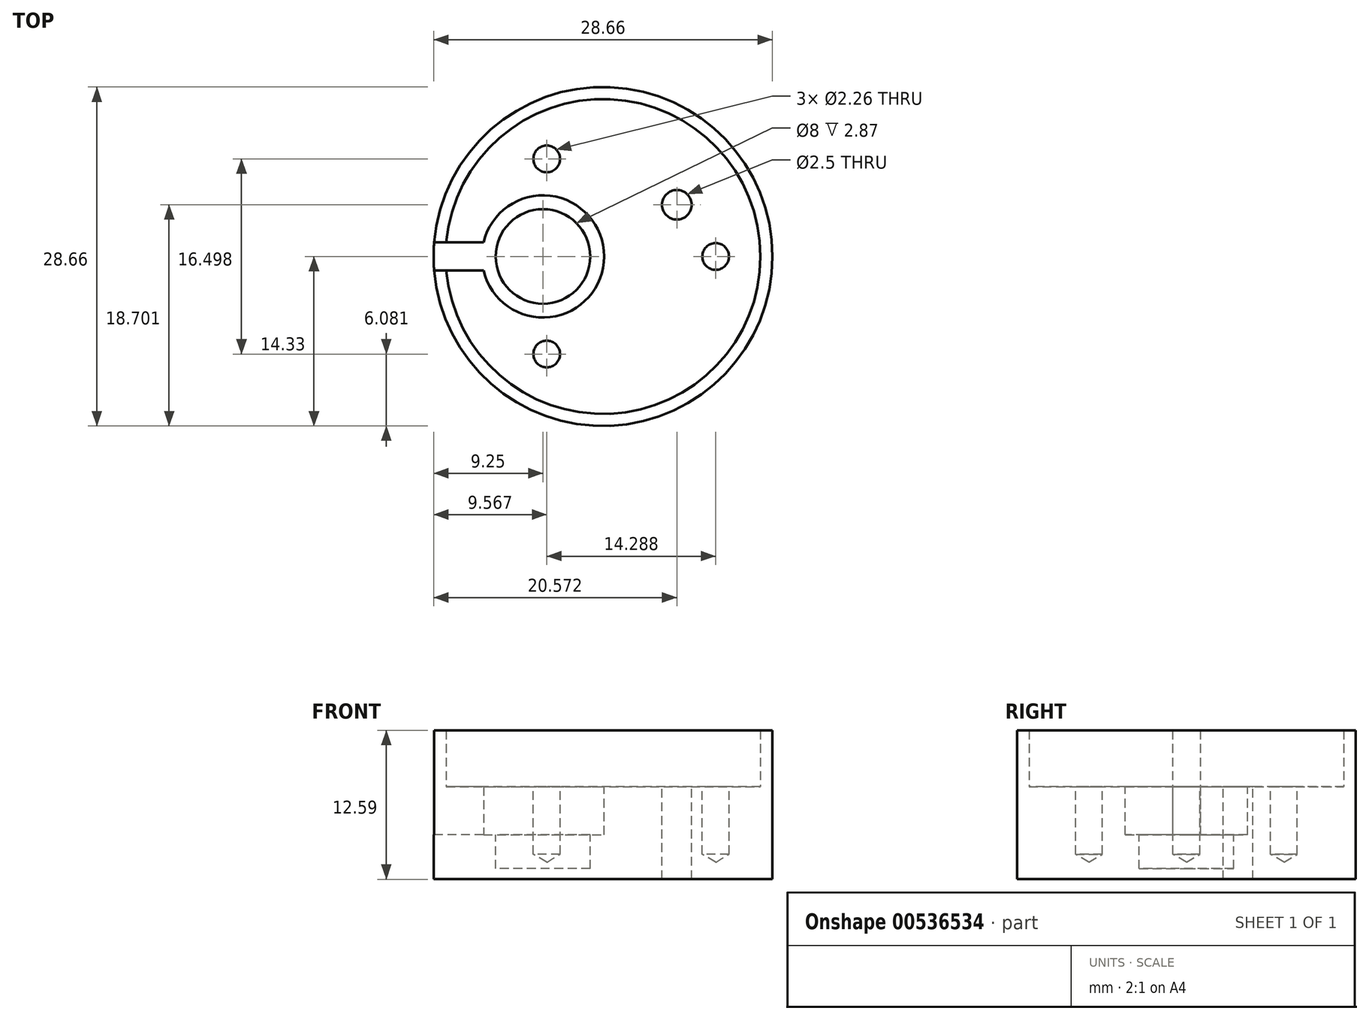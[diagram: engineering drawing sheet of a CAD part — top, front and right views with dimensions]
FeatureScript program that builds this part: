
annotation { "Feature Type Name" : "Feature", "Feature Type Description" : "" }
export const myFeature = defineFeature(function(context is Context, id is Id, definition is map)
    precondition{}
    {
        {
            var Q0;
            Q0=qCreatedBy(makeId("Front.planeOp"),FACE);
            var sketch = newSketch(context, id + "F0", { "sketchPlane" : qUnion([Q0])});
            skLineSegment(sketch, "E0", {"start": v(14.33, 0) * mm, "end": v(14.33, -12.59) * mm});
            skLineSegment(sketch, "E1", {"start": v(14.33, -12.59) * mm, "end": v(0, -12.59) * mm});
            skLineSegment(sketch, "E2", {"start": v(0, -12.59) * mm, "end": v(0, -4.76) * mm});
            skLineSegment(sketch, "E3", {"start": v(0, -4.76) * mm, "end": v(13.31, -4.76) * mm});
            skLineSegment(sketch, "E4", {"start": v(13.31, -4.76) * mm, "end": v(13.31, 0) * mm});
            skLineSegment(sketch, "E5", {"start": v(13.31, 0) * mm, "end": v(14.33, 0) * mm});
            skLineSegment(sketch, "E6", {"start": v(0, -12.59) * mm, "end": v(0, -26.31) * mm, "construction": true});
            skSolve(sketch);
        }
        {
            var Q0;
            Q0=qSketchRegion(id+"F0",true);
            var Q1;
            Q1=sQuery(id+"F0.wireOp",EDGE,"E2");
            revolve(context, id + "F1", {"entities" : qUnion([Q0]), "axis" : qUnion([Q1]), "revolveType" : RevolveType.FULL});
        }
        {
            var Q0;
            Q0=makeQuery(id+"F1.opRevolve","SWEPT_FACE",FACE,{"disambiguationData":[OSD([sQuery(id+"F0.wireOp",EDGE,"E3")])]});
            var sketch = newSketch(context, id + "F2", { "sketchPlane" : qUnion([Q0])});
            skPoint(sketch, "E7", {"position": v(9.52, 0) * mm});
            skPoint(sketch, "E8.1.0", {"position": v(-4.76, 8.25) * mm});
            skPoint(sketch, "E8.2.0", {"position": v(-4.76, -8.25) * mm});
            skPoint(sketch, "E8.center", {"position": v(0, 0) * mm});
            skSolve(sketch);
        }
        {
            var Q0;
            Q0=sQuery(id+"F2.wireOp",VERTEX,"E7");
            var Q1;
            Q1=sQuery(id+"F2.wireOp",VERTEX,"E8.1.0");
            var Q2;
            Q2=sQuery(id+"F2.wireOp",VERTEX,"E8.2.0");
            var Q3;
            Q3=makeQuery(id+"F1.opRevolve","SWEPT_BODY",BODY,{"disambiguationData":[OSD([sQuery(id+"F0.wireOp",EDGE,"E0"),sQuery(id+"F0.wireOp",EDGE,"E1"),sQuery(id+"F0.wireOp",EDGE,"E2"),sQuery(id+"F0.wireOp",EDGE,"E3"),sQuery(id+"F0.wireOp",EDGE,"E4"),sQuery(id+"F0.wireOp",EDGE,"E5"),sQuery(id+"F0.wireOp",EDGE,"N4qPm8u9-ntjg-4JQa-pogc-oRLvVNEznxfI"),sQuery(id+"F0.wireOp",EDGE,"MrgsN7Nr-Gjff-1Huv-wU94-kZHdJzqhYVDD"),sQuery(id+"F0.wireOp",EDGE,"Pg9PKC79-TiTN-lwUD-c8gR-E9RlHLgOT5QF"),sQuery(id+"F0.wireOp",EDGE,"fodt5jp9-1a0J-tqfQ-503d-72WKcELB2Erp")])]});
            hole(context, id + "F3", {"style" : HoleStyle.SIMPLE, "endStyle" : HoleEndStyle.BLIND, "standardTappedOrClearance" : lookupTablePath({ "standard" : "ANSI", "engagement" : "75%", "pitch" : "40 tpi", "size" : "#4", "type" : "Tapped" }), "standardBlindInLast" : lookupTablePath({ "standard" : "ANSI", "engagement" : "75%", "pitch" : "40 tpi", "size" : "#4", "type" : "Tapped" }), "holeDiameter" : 2.26 * mm, "majorDiameter" : 2.84 * mm, "showTappedDepth" : true, "holeDepth" : 5.72 * mm, "tappedDepth" : 5.08 * mm, "tapClearance" : 1, "startFromSketch" : true, "locations" : qUnion([Q0, Q1, Q2]), "scope" : qUnion([Q3])});
        }
        {
            var Q0;
            Q0=makeQuery(id+"F1.opRevolve","SWEPT_FACE",FACE,{"disambiguationData":[OSD([sQuery(id+"F0.wireOp",EDGE,"E3")])]});
            var sketch = newSketch(context, id + "F4", { "sketchPlane" : qUnion([Q0])});
            skLineSegment(sketch, "E9", {"start": v(0, 0) * mm, "end": v(-5.08, 0) * mm, "construction": true});
            skCircle(sketch, "E10", {"center": v(-5.08, 0) * mm, "radius": 5.17 * mm});
            skSolve(sketch);
        }
        {
            var Q0;
            Q0 = qSketchRegion(id + "F4", true);
            extrude(context, id + "F5", {"entities" : qUnion([Q0]), "operationType" : NewBodyOperationType.REMOVE, "oppositeDirection" : true, "depth" : 4.06 * mm, "offsetDistance" : 25.4 * mm});
        }
        {
            var Q0;
            Q0=makeQuery(id+"F5.boolean.opBoolean","COPY",FACE,{"derivedFrom":makeQuery(id+"F5.opExtrude","CAP_FACE",FACE,{"disambiguationData":[OSD([sQuery(id+"F4.wireOp",EDGE,"E10")])],"isStart":false})});
            var sketch = newSketch(context, id + "F6", { "sketchPlane" : qUnion([Q0])});
            skPoint(sketch, "E11", {"position": v(-5.08, 0) * mm});
            skCircle(sketch, "E12", {"center": v(-5.08, 0) * mm, "radius": 4 * mm});
            skSolve(sketch);
        }
        {
            var Q0;
            Q0=makeQuery(id+"F6.imprint","IMPRINT",FACE,{"disambiguationData":[TD([[makeQuery(id+"F6.imprint","IMPRINT",EDGE,{"derivedFrom":sQuery(id+"F6.wireOp",EDGE,"E12")}),1.0]])]});
            extrude(context, id + "F7", {"entities" : qUnion([Q0]), "operationType" : NewBodyOperationType.REMOVE, "oppositeDirection" : true, "depth" : 2.87 * mm, "offsetDistance" : 25.4 * mm});
        }
        {
            var Q0;
            Q0=makeQuery(id+"F5.boolean.opBoolean","COPY",FACE,{"derivedFrom":makeQuery(id+"F5.opExtrude","CAP_FACE",FACE,{"disambiguationData":[OSD([sQuery(id+"F4.wireOp",EDGE,"E10")])],"isStart":false})});
            var sketch = newSketch(context, id + "F8", { "sketchPlane" : qUnion([Q0])});
            skLineSegment(sketch, "E13.bottom", {"start": v(-10.1, 1.2) * mm, "end": v(-15.53, 1.2) * mm});
            skLineSegment(sketch, "E13.top", {"start": v(-10.1, -1.2) * mm, "end": v(-15.53, -1.2) * mm});
            skLineSegment(sketch, "E13.left", {"start": v(-10.1, 1.2) * mm, "end": v(-10.1, -1.2) * mm});
            skLineSegment(sketch, "E13.right", {"start": v(-15.53, 1.2) * mm, "end": v(-15.53, -1.2) * mm});
            skPoint(sketch, "E14", {"position": v(-10.1, 0) * mm});
            skSolve(sketch);
        }
        {
            var Q0;
            {var subQ0=sQuery(id+"F8.wireOp",EDGE,"E13.bottom");Q0=makeQuery(id+"F8.imprint","IMPRINT",FACE,{"disambiguationData":[TD([[makeQuery(id+"F8.imprint","IMPRINT",EDGE,{"derivedFrom":subQ0}),1.0]])]});}
            extrude(context, id + "F9", {"entities" : qUnion([Q0]), "operationType" : NewBodyOperationType.REMOVE, "depth" : 25.4 * mm, "offsetDistance" : 25.4 * mm});
        }
        {
            var Q0;
            Q0=makeQuery(id+"F1.opRevolve","SWEPT_FACE",FACE,{"disambiguationData":[OSD([sQuery(id+"F0.wireOp",EDGE,"E3")])]});
            var sketch = newSketch(context, id + "F10", { "sketchPlane" : qUnion([Q0])});
            skLineSegment(sketch, "E15", {"start": v(0, 0) * mm, "end": v(6.24, 4.37) * mm, "construction": true});
            skSolve(sketch);
        }
        {
            var Q0;
            Q0=sQuery(id+"F10.wireOp",VERTEX,"E15.end");
            var Q1;
            Q1=makeQuery(id+"F1.opRevolve","SWEPT_BODY",BODY,{"disambiguationData":[OSD([sQuery(id+"F0.wireOp",EDGE,"E0"),sQuery(id+"F0.wireOp",EDGE,"E1"),sQuery(id+"F0.wireOp",EDGE,"E2"),sQuery(id+"F0.wireOp",EDGE,"E3"),sQuery(id+"F0.wireOp",EDGE,"E4"),sQuery(id+"F0.wireOp",EDGE,"E5")])]});
            hole(context, id + "F11", {"style" : HoleStyle.SIMPLE, "endStyle" : HoleEndStyle.THROUGH, "standardTappedOrClearance" : lookupTablePath({ "standard" : "ISO", "engagement" : "75%", "pitch" : "0.5 mm", "size" : "M3", "type" : "Tapped" }), "standardBlindInLast" : lookupTablePath({ "standard" : "ISO", "engagement" : "75%", "pitch" : "0.5 mm", "size" : "M3", "type" : "Tapped" }), "holeDiameter" : 2.5 * mm, "majorDiameter" : 3 * mm, "showTappedDepth" : true, "tappedDepth" : 9.52 * mm, "tapClearance" : 1, "startFromSketch" : true, "locations" : qUnion([Q0]), "scope" : qUnion([Q1])});
        }
    });
